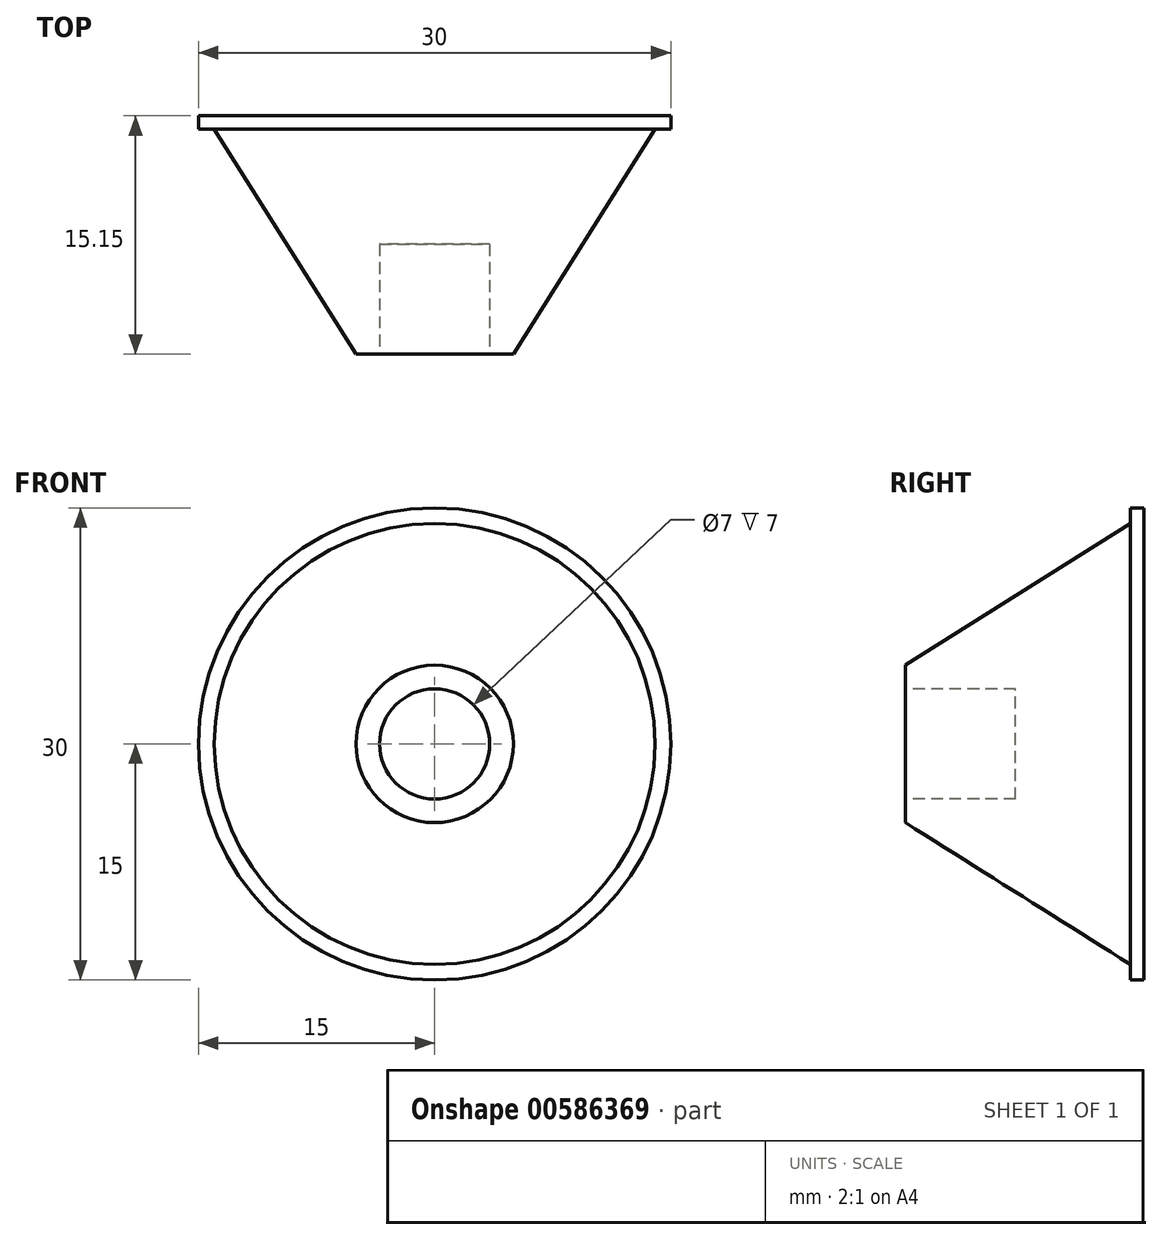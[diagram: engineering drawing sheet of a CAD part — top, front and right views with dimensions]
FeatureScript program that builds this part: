
annotation { "Feature Type Name" : "Feature", "Feature Type Description" : "" }
export const myFeature = defineFeature(function(context is Context, id is Id, definition is map)
    precondition{}
    {
        {
            var Q0;
            Q0=qCreatedBy(makeId("Front.planeOp"),FACE);
            var sketch = newSketch(context, id + "F0", { "sketchPlane" : qUnion([Q0])});
            skCircle(sketch, "E0", {"center": v(0, 0) * mm, "radius": 14 * mm});
            skCircle(sketch, "E1", {"center": v(0, 0) * mm, "radius": 15 * mm});
            skSolve(sketch);
        }
        {
            var Q0;
            Q0 = qSketchRegion(id + "F0", true);
            var Q1;
            Q1=makeQuery(id+"F0.imprint","IMPRINT",FACE,{"disambiguationData":[TD([[makeQuery(id+"F0.imprint","IMPRINT",EDGE,{"derivedFrom":sQuery(id+"F0.wireOp",EDGE,"E0")}),1.0]])]});
            extrude(context, id + "F1", {"entities" : qUnion([Q0, Q1]), "depth" : .85 * mm, "offsetDistance" : 25 * mm});
        }
        {
            var Q0;
            Q0=makeQuery(id+"F1.opExtrude","CAP_FACE",FACE,{"disambiguationData":[OSD([sQuery(id+"F0.wireOp",EDGE,"E1")])],"isStart":false});
            cPlane(context, id + "F2", {"entities" : qUnion([Q0]), "cplaneType" : CPlaneType.OFFSET, "offset" : 14.3 * mm, "width" : 150 * mm, "height" : 150 * mm});
        }
        {
            var Q0;
            Q0=qCreatedBy(id+"F2.planeOp",FACE);
            var sketch = newSketch(context, id + "F3", { "sketchPlane" : qUnion([Q0])});
            skCircle(sketch, "E2", {"center": v(0, 0) * mm, "radius": 5 * mm});
            skSolve(sketch);
        }
        {
            var Q0;
            Q0=makeQuery(id+"F1.opExtrude","CAP_FACE",FACE,{"disambiguationData":[OSD([sQuery(id+"F0.wireOp",EDGE,"E1")])],"isStart":false});
            var sketch = newSketch(context, id + "F4", { "sketchPlane" : qUnion([Q0])});
            skCircle(sketch, "E3", {"center": v(0, 0) * mm, "radius": 14 * mm});
            skSolve(sketch);
        }
        {
            var Q0;
            Q0=makeQuery(id+"F4.imprint","IMPRINT",FACE,{"disambiguationData":[TD([[makeQuery(id+"F4.imprint","IMPRINT",EDGE,{"derivedFrom":sQuery(id+"F4.wireOp",EDGE,"E3")}),1.0]])]});
            var Q1;
            Q1=makeQuery(id+"F3.imprint","IMPRINT",FACE,{"disambiguationData":[TD([[makeQuery(id+"F3.imprint","IMPRINT",EDGE,{"derivedFrom":sQuery(id+"F3.wireOp",EDGE,"E2")}),1.0]])]});
            loft(context, id + "F5", {"operationType" : NewBodyOperationType.ADD, "sheetProfilesArray" : [{ "sheetProfileEntities" : qUnion([Q0]) }, { "sheetProfileEntities" : qUnion([Q1]) }]});
        }
        {
            var Q0;
            Q0=makeQuery(id+"F3.imprint","IMPRINT",FACE,{"disambiguationData":[TD([[makeQuery(id+"F3.imprint","IMPRINT",EDGE,{"derivedFrom":sQuery(id+"F3.wireOp",EDGE,"E2")}),1.0]])]});
            var sketch = newSketch(context, id + "F6", { "sketchPlane" : qUnion([Q0])});
            skCircle(sketch, "E4", {"center": v(0, 0) * mm, "radius": 3.5 * mm});
            skSolve(sketch);
        }
        {
            var Q0;
            Q0 = qSketchRegion(id + "F6", true);
            extrude(context, id + "F7", {"entities" : qUnion([Q0]), "operationType" : NewBodyOperationType.REMOVE, "oppositeDirection" : true, "depth" : 7 * mm, "offsetDistance" : 25 * mm});
        }
    });
